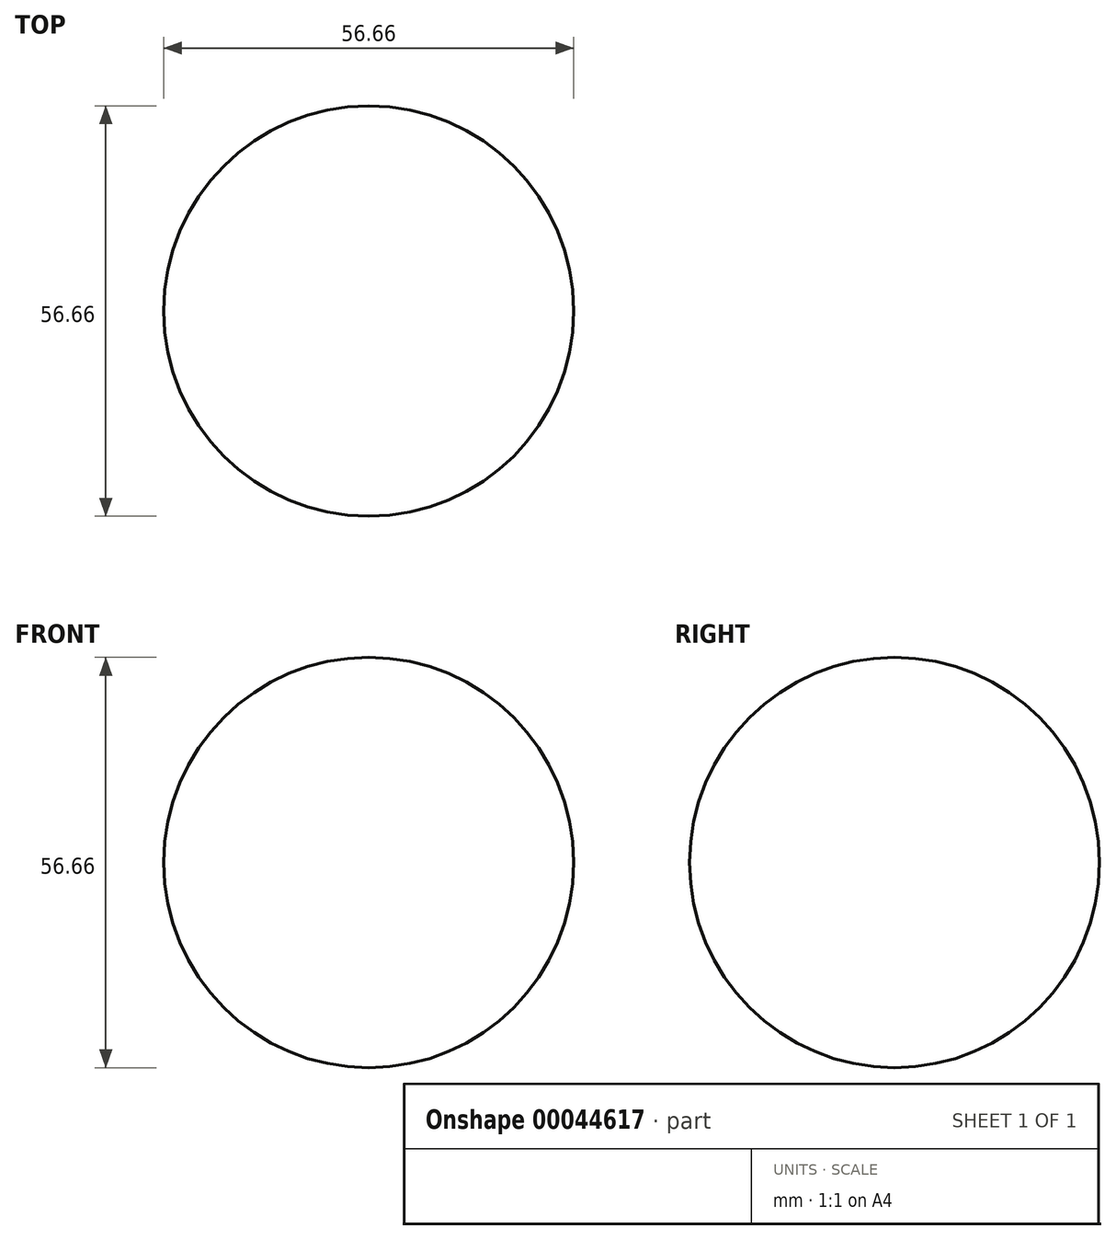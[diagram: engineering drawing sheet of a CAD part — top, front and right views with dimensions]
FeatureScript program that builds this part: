
annotation { "Feature Type Name" : "Feature", "Feature Type Description" : "" }
export const myFeature = defineFeature(function(context is Context, id is Id, definition is map)
    precondition{}
    {
        {
            var Q0;
            Q0=qCreatedBy(makeId("Front.planeOp"),FACE);
            var sketch = newSketch(context, id + "F0", { "sketchPlane" : qUnion([Q0])});
            skCircle(sketch, "E0", {"center": v(0, 0) * mm, "radius": 28.33 * mm});
            skLineSegment(sketch, "E1", {"start": v(-28.33, 0) * mm, "end": v(28.33, 0) * mm});
            skSolve(sketch);
        }
        {
            var Q0;
            {var subQ0=sQuery(id+"F0.wireOp",EDGE,"E1");Q0=makeQuery(id+"F0.imprint","IMPRINT",FACE,{"disambiguationData":[TD([[makeQuery(id+"F0.imprint","IMPRINT",EDGE,{"derivedFrom":subQ0}),-1.0]])]});}
            var Q1;
            Q1=sQuery(id+"F0.wireOp",EDGE,"E1");
            revolve(context, id + "F1", {"entities" : qUnion([Q0]), "axis" : qUnion([Q1]), "revolveType" : RevolveType.FULL});
        }
        {
            var Q0;
            Q0=qCreatedBy(makeId("Front.planeOp"),FACE);
            var sketch = newSketch(context, id + "F2", { "sketchPlane" : qUnion([Q0])});
            skFitSpline(sketch, "E2", {"points": [v(19.94, 20.03) * mm, v(11.72, -11.54) * mm, v(-12.5, -12.32) * mm, v(-19.94, 20.18) * mm, v(0, 35.5) * mm, v(19.94, 20.03) * mm]});
            skFitSpline(sketch, "E3", {"points": [v(-18.45, 18.69) * mm, v(-10.55, -10.37) * mm, v(9.66, -9.48) * mm, v(17.66, 17.75) * mm, v(0, 32.41) * mm, v(-18.45, 18.69) * mm]});
            skSolve(sketch);
        }
        {
            var Q0;
            Q0=sQuery(id+"F2.wireOp",EDGE,"E2");
            var Q1;
            Q1=sQuery(id+"F2.wireOp",EDGE,"E3");
            extrude(context, id + "F3", {"bodyType" : ToolBodyType.SURFACE, "surfaceEntities" : qUnion([Q0, Q1]), "endBound" : BoundingType.UP_TO_NEXT, "depth" : 25.4 * mm});
        }
        {
            var Q0;
            Q0=sQuery(id+"F2.wireOp",EDGE,"E2");
            var Q1;
            Q1=sQuery(id+"F2.wireOp",EDGE,"E3");
            extrude(context, id + "F4", {"bodyType" : ToolBodyType.SURFACE, "surfaceEntities" : qUnion([Q0, Q1]), "endBound" : BoundingType.UP_TO_NEXT, "depth" : 25.4 * mm, "hasSecondDirection" : true, "secondDirectionOppositeDirection" : true, "secondDirectionDepth" : 25.4 * mm});
        }
        {
            var Q0;
            Q0=qCreatedBy(makeId("Right.planeOp"),FACE);
            var sketch = newSketch(context, id + "F5", { "sketchPlane" : qUnion([Q0])});
            skCircle(sketch, "E4", {"center": v(0, 0) * mm, "radius": 29.17 * mm});
            skSolve(sketch);
        }
        {
            var Q0;
            Q0=sQuery(id+"F5.wireOp",EDGE,"E4");
            extrude(context, id + "F6", {"bodyType" : ToolBodyType.SURFACE, "surfaceEntities" : qUnion([Q0]), "depth" : 0.03 * mm});
        }
    });
